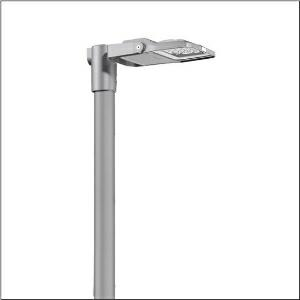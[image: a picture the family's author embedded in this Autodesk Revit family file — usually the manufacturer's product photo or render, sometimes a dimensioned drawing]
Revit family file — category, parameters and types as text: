
# Revit family: floodlight_fl_21_iq_micro___pl52_5xa7762a4d3a_1d61
name_source: partatom
category: Lighting Fixtures
units: mm (PartAtom-declared; Revit-internal decimal feet)

## family parameters
Cut with Voids When Loaded = No
Host = Face
Light Source = No
Part Type = Normal
Room Calculation Point = No
Round Connector Dimension = Use Diameter
Shared = No

## types (1)
- --- (1 x LED, 3010 lm, 23.1 W, 4000K)
    Apparent Load = 23 VA
    CIE Flux Codes = 26 60 98 100 100
    Color Rendering = 70
    Color Temperature = 4000K
    Default Elevation = 1800 mm
    Description = Floodlight FL 21 iQ micro, floodlight, primary light control with lens, of PMMA, primary optical cover: protective disc, of toughened safety glass, transparent, light distribution: PL52, light emission: direct distribution, installation type: surface-mounted, LED, High Power LED, rated luminous flux: 3.010lm, luminous efficacy: 130lm/W, light colour: 740, colour temperature: 4000K, control gear: iQ Street-Remote/DALI, control: Auto-Match, Temp-Guard, Night-Set, Smart-Wire, Desk-Remote (wireless, voltage-free reading and setting of iQ features in the workshop via application-optimized NFC function/RFID function), optimised constant luminous flux control (CLO 2.0), Street-Remote, with terminal, 6-pole, mains connection: 220..240V, AC, 50/60Hz, start of lifetime: 23W, end of service life: 24W, reduction: 11W, luminaire housing, of diecast aluminium, powder-coated, Siteco® metallic grey (DB 702S), corrosivity category C5 mid according to DIN EN ISO 12944, suitable for swimming pools, chlorine-resistant, sealing non-destructively replaceable, please order mast flange separately, mast bracket, of steel, galvanised, powder-coated, Siteco® metallic grey (DB 702S), protection rating (complete): IP66, insulation class (complete): insulation class II (safety insulation), certification: CE, ENEC, VDE, protection symbol: D, impact resistance: IK07, permissible operating ambient temperature: -40..+40°C, permissible operating ambient temperature for outdoor applications: -40..+50°C, standard: DIN EN 12944, LABS conformity tested according to VDMA 24364:2018-05, packaging unit: 1 piece

Light Distribution: PL52
    Height = 65 mm
    Lamp = 1 x LED
    Lamp Light Flux = 3010 lm
    Lamp Power = 23.1 W
    Lamp count = 1
    Length = 312 mm
    Luminous efficacy = 130 lm/W
    Manufacturer = Siteco
    ModVariant = No
    Model = 5XA7762A4D3A
    Number of Poles = 1
    OnlyDefault = Yes
    Power Factor = 1
    Product Name = Floodlight FL 21 iQ micro | PL52
    Product group = floodlight | pylon annexe
    ProductGroupID = 6200
    Protection Class = Protection class II
    Protection Degree = IP 66
    RLX_Detail_Level = 1
    RLX_Emergency_Light_Flux = 0 lm
    RLX_Emergency_Type = 0
    RLX_Emergency_Type_DB = No
    RlxData = <blob elided: 102085 chars, md5=f54618a1>
    Socket = socket
    Standby Power = 0 W
    System Light Flux = 3010 lm
    System Power = 23 W
    Type Comments = factory setting: luminous flux: 100 % | dim-lin: 254 | 455 mA
    Type Image = l_1007121.jpg
    URL = http://relux.com
    VarID = @adj_177738
    Voltage = 0 V
    Weight = 0.00 kg
    Width = 230 mm

## geometry (parser evidence)
native form markers: Blend x4, Sweep x13
no freeform markers — native parametric forms only
